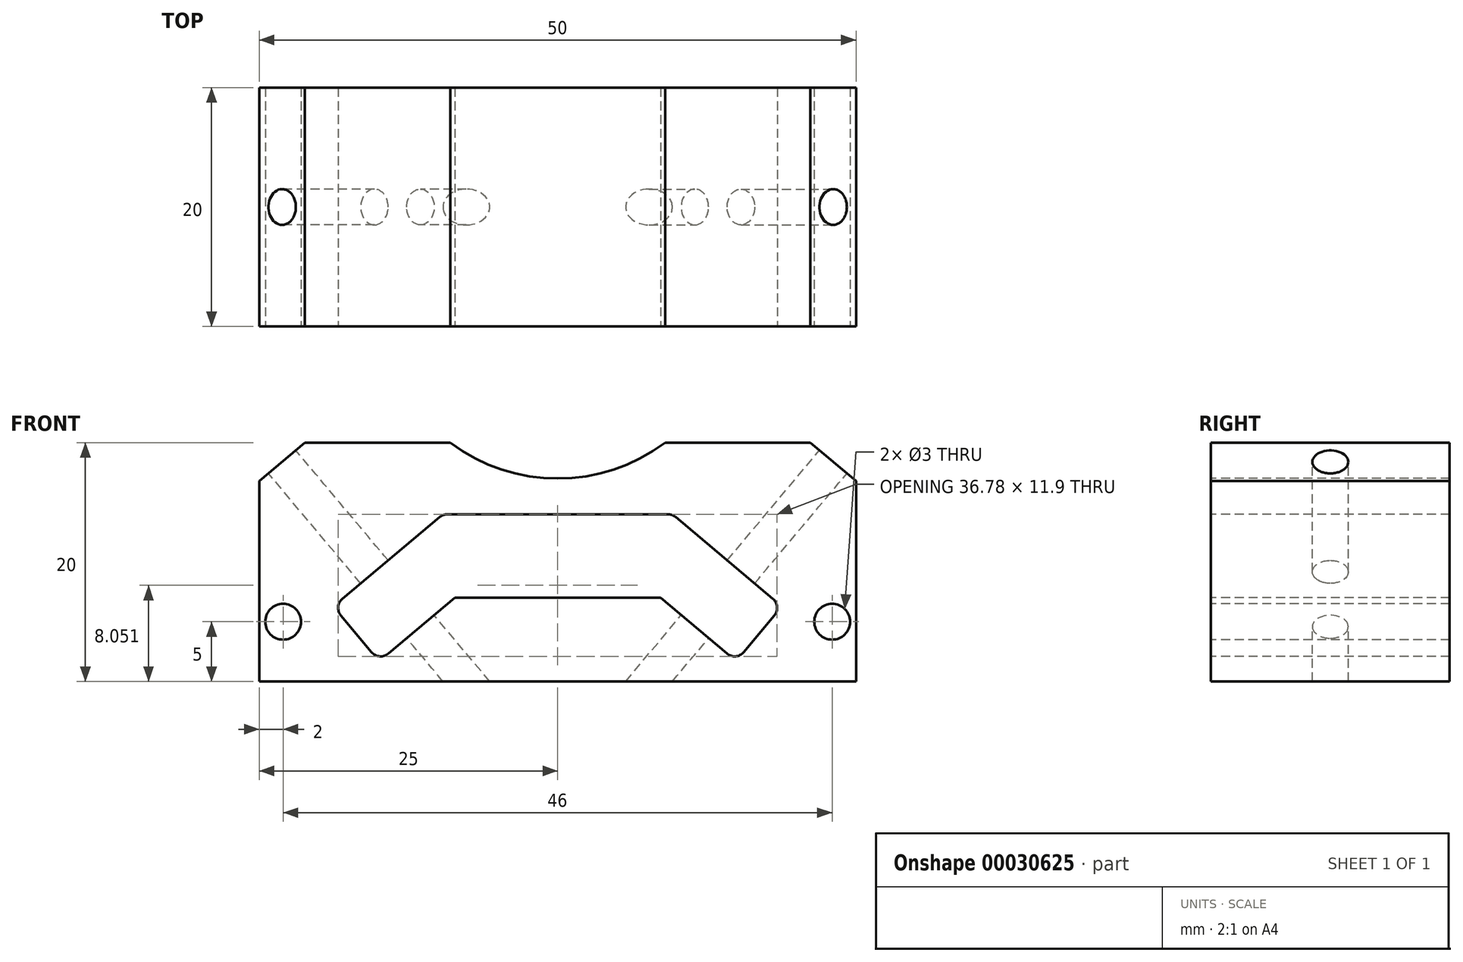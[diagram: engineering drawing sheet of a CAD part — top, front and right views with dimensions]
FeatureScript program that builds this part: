
annotation { "Feature Type Name" : "Feature", "Feature Type Description" : "" }
export const myFeature = defineFeature(function(context is Context, id is Id, definition is map)
    precondition{}
    {
        {
            var Q0;
            Q0=qCreatedBy(makeId("Front.planeOp"),FACE);
            var sketch = newSketch(context, id + "F0", { "sketchPlane" : qUnion([Q0])});
            skLineSegment(sketch, "E0.rect.bottom", {"start": v(25, -10) * mm, "end": v(-25, -10) * mm});
            skLineSegment(sketch, "E0.rect.top", {"start": v(21.17, 10) * mm, "end": v(9, 10) * mm});
            skLineSegment(sketch, "E0.rect.left", {"start": v(25, -10) * mm, "end": v(25, 6.79) * mm});
            skLineSegment(sketch, "E0.rect.right", {"start": v(-25, -10) * mm, "end": v(-25, 6.79) * mm});
            skPoint(sketch, "E0.rect.middle", {"position": v(0, 0) * mm});
            skLineSegment(sketch, "E1", {"start": v(-21.17, 10) * mm, "end": v(-25, 6.79) * mm});
            skLineSegment(sketch, "E2.MirrorCS", {"start": v(21.17, 10) * mm, "end": v(25, 6.79) * mm});
            skArc(sketch, "E3", {"start": v(0, 7) * mm, "mid": v(-4.74, 7.77) * mm, "end": v(-9, 10) * mm});
            skArc(sketch, "E4.MirrorCS", {"start": v(0, 7) * mm, "mid": v(4.74, 7.77) * mm, "end": v(9, 10) * mm});
            skPoint(sketch, "E5.orphan", {"position": v(-25, 10) * mm});
            skPoint(sketch, "E6.orphan", {"position": v(25, 10) * mm});
            skLineSegment(sketch, "E7.trimOffspring", {"start": v(-9, 10) * mm, "end": v(-21.17, 10) * mm});
            skCircle(sketch, "E8", {"center": v(-23, -5) * mm, "radius": 1.5 * mm});
            skCircle(sketch, "E9.MirrorC", {"center": v(23, -5) * mm, "radius": 1.5 * mm});
            skLineSegment(sketch, "E10", {"start": v(-21.94, 9.36) * mm, "end": v(-5.7, -10) * mm});
            skLineSegment(sketch, "E11", {"start": v(-24.23, 7.43) * mm, "end": v(-9.6, -10) * mm});
            skLineSegment(sketch, "E12.MirrorCS", {"start": v(21.94, 9.36) * mm, "end": v(5.7, -10) * mm});
            skLineSegment(sketch, "E13.MirrorCS", {"start": v(24.23, 7.43) * mm, "end": v(9.6, -10) * mm});
            skLineSegment(sketch, "E14", {"start": v(0, 4) * mm, "end": v(-9.24, 4) * mm});
            skLineSegment(sketch, "E15", {"start": v(-9.89, 3.77) * mm, "end": v(-18.03, -3.07) * mm});
            skLineSegment(sketch, "E16", {"start": v(-18.16, -4.48) * mm, "end": v(-15.59, -7.54) * mm});
            skLineSegment(sketch, "E17", {"start": v(-14.18, -7.67) * mm, "end": v(-8.62, -3) * mm});
            skLineSegment(sketch, "E18", {"start": v(-8.62, -3) * mm, "end": v(0, -3) * mm});
            skLineSegment(sketch, "E19.MirrorCS", {"start": v(14.18, -7.67) * mm, "end": v(8.62, -3) * mm});
            skLineSegment(sketch, "E20.MirrorCS", {"start": v(18.16, -4.48) * mm, "end": v(15.59, -7.54) * mm});
            skLineSegment(sketch, "E21.MirrorCS", {"start": v(9.89, 3.77) * mm, "end": v(18.03, -3.07) * mm});
            skLineSegment(sketch, "E22.MirrorCS", {"start": v(8.62, -3) * mm, "end": v(0, -3) * mm});
            skLineSegment(sketch, "E23.MirrorCS", {"start": v(0, 4) * mm, "end": v(9.24, 4) * mm});
            skPoint(sketch, "E24.visualSharp", {"position": v(-14.94, -8.3) * mm});
            skArc(sketch, "E24.filletArc", {"start": v(-15.59, -7.54) * mm, "mid": v(-14.9, -7.9) * mm, "end": v(-14.18, -7.67) * mm});
            skPoint(sketch, "E25.visualSharp", {"position": v(-18.8, -3.71) * mm});
            skArc(sketch, "E25.filletArc", {"start": v(-18.03, -3.07) * mm, "mid": v(-18.39, -3.75) * mm, "end": v(-18.16, -4.48) * mm});
            skPoint(sketch, "E26.visualSharp", {"position": v(-9.6, 4) * mm});
            skArc(sketch, "E26.filletArc", {"start": v(-9.24, 4) * mm, "mid": v(-9.59, 3.94) * mm, "end": v(-9.89, 3.77) * mm});
            skPoint(sketch, "E27.visualSharp", {"position": v(9.6, 4) * mm});
            skArc(sketch, "E27.filletArc", {"start": v(9.89, 3.77) * mm, "mid": v(9.59, 3.94) * mm, "end": v(9.24, 4) * mm});
            skPoint(sketch, "E28.visualSharp", {"position": v(18.8, -3.71) * mm});
            skArc(sketch, "E28.filletArc", {"start": v(18.16, -4.48) * mm, "mid": v(18.39, -3.75) * mm, "end": v(18.03, -3.07) * mm});
            skPoint(sketch, "E29.visualSharp", {"position": v(14.94, -8.3) * mm});
            skArc(sketch, "E29.filletArc", {"start": v(14.18, -7.67) * mm, "mid": v(14.9, -7.9) * mm, "end": v(15.59, -7.54) * mm});
            skSolve(sketch);
        }
        {
            var Q0;
            Q0 = qSketchRegion(id + "F0", true);
            extrude(context, id + "F1", {"entities" : qUnion([Q0]), "endBound" : BoundingType.SYMMETRIC, "oppositeDirection" : true, "depth" : 20 * mm});
        }
        {
            var Q0;
            Q0=makeQuery(id+"F1.opExtrude","SWEPT_FACE",FACE,{"disambiguationData":[OSD([sQuery(id+"F0.wireOp",EDGE,"E1")])]});
            var sketch = newSketch(context, id + "F2", { "sketchPlane" : qUnion([Q0])});
            skCircle(sketch, "E30", {"center": v(-12.29, 0) * mm, "radius": 1.5 * mm});
            skSolve(sketch);
        }
        {
            var Q0;
            Q0 = qSketchRegion(id + "F2", true);
            extrude(context, id + "F3", {"entities" : qUnion([Q0]), "operationType" : NewBodyOperationType.REMOVE, "endBound" : BoundingType.THROUGH_ALL, "oppositeDirection" : true, "depth" : 25 * mm});
        }
        {
            var Q0;
            Q0=makeQuery(id+"F1.opExtrude","SWEPT_FACE",FACE,{"disambiguationData":[OSD([sQuery(id+"F0.wireOp",EDGE,"E2.MirrorCS")])]});
            var sketch = newSketch(context, id + "F4", { "sketchPlane" : qUnion([Q0])});
            skCircle(sketch, "E31", {"center": v(12.29, 0) * mm, "radius": 1.5 * mm});
            skSolve(sketch);
        }
        {
            var Q0;
            Q0 = qSketchRegion(id + "F4", true);
            extrude(context, id + "F5", {"entities" : qUnion([Q0]), "operationType" : NewBodyOperationType.REMOVE, "endBound" : BoundingType.THROUGH_ALL, "oppositeDirection" : true, "depth" : 25 * mm});
        }
    });
